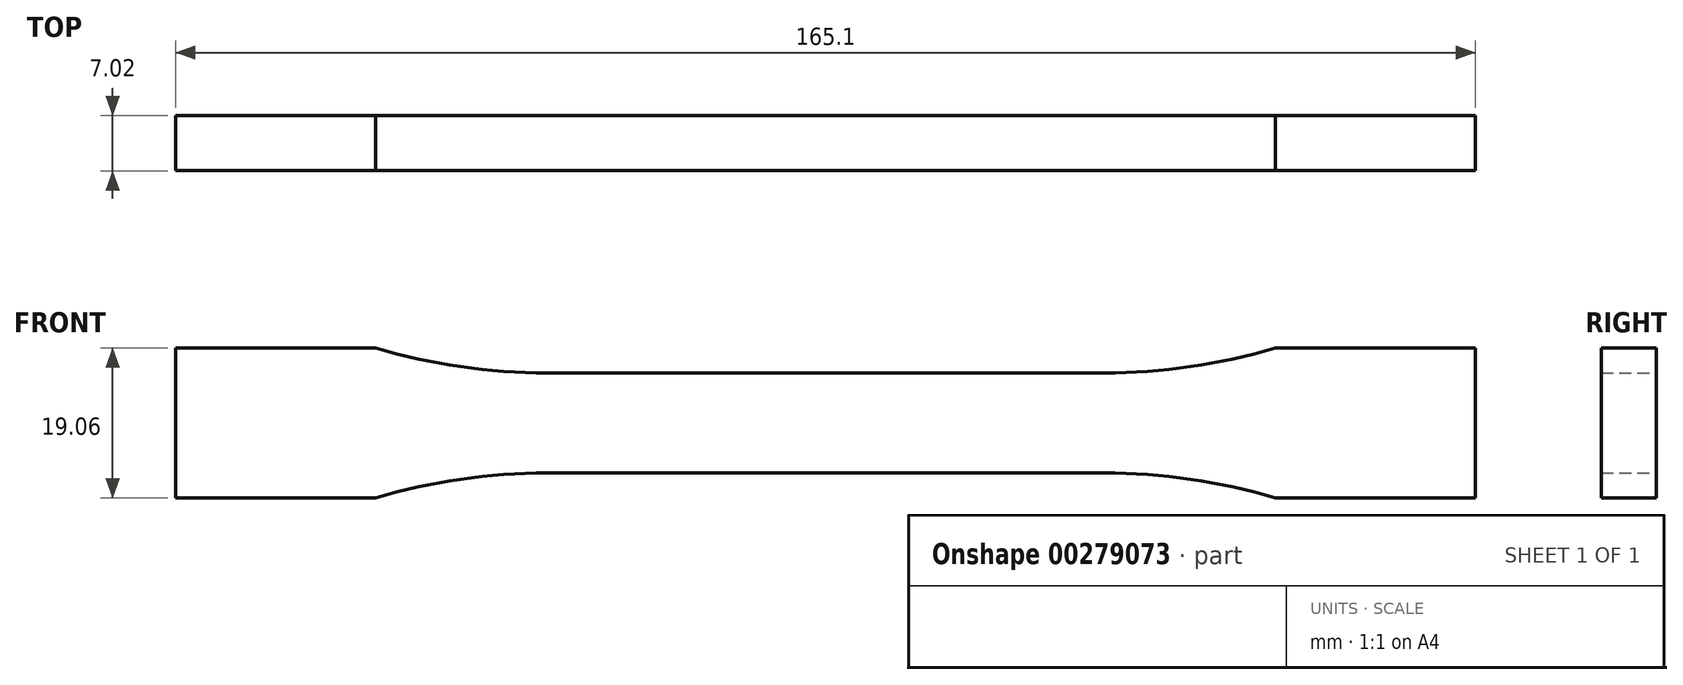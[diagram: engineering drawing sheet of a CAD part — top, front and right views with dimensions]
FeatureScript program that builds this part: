
annotation { "Feature Type Name" : "Feature", "Feature Type Description" : "" }
export const myFeature = defineFeature(function(context is Context, id is Id, definition is map)
    precondition{}
    {
        {
            var Q0;
            Q0=qCreatedBy(makeId("Front.planeOp"),FACE);
            var sketch = newSketch(context, id + "F0", { "sketchPlane" : qUnion([Q0])});
            skLineSegment(sketch, "E0", {"start": v(0, 6.35) * mm, "end": v(35.38, 6.35) * mm});
            skArc(sketch, "E1", {"start": v(35.38, 6.35) * mm, "mid": v(46.38, 7.15) * mm, "end": v(57.15, 9.53) * mm});
            skLineSegment(sketch, "E2", {"start": v(57.15, 9.53) * mm, "end": v(82.55, 9.53) * mm});
            skLineSegment(sketch, "E3.MirrorCS", {"start": v(57.15, -9.53) * mm, "end": v(82.55, -9.53) * mm});
            skLineSegment(sketch, "E4.MirrorCS", {"start": v(0, -6.35) * mm, "end": v(35.38, -6.35) * mm});
            skArc(sketch, "E5.MirrorCS", {"start": v(35.38, -6.35) * mm, "mid": v(46.38, -7.15) * mm, "end": v(57.15, -9.53) * mm});
            skArc(sketch, "E6.MirrorCS", {"start": v(-35.38, -6.35) * mm, "mid": v(-46.38, -7.15) * mm, "end": v(-57.15, -9.53) * mm});
            skLineSegment(sketch, "E7.MirrorCS", {"start": v(0, 6.35) * mm, "end": v(-35.38, 6.35) * mm});
            skArc(sketch, "E8.MirrorCS", {"start": v(-35.38, 6.35) * mm, "mid": v(-46.38, 7.15) * mm, "end": v(-57.15, 9.53) * mm});
            skLineSegment(sketch, "E9.MirrorCS", {"start": v(-57.15, -9.53) * mm, "end": v(-82.55, -9.53) * mm});
            skLineSegment(sketch, "E10.MirrorCS", {"start": v(0, -6.35) * mm, "end": v(-35.38, -6.35) * mm});
            skLineSegment(sketch, "E11.MirrorCS", {"start": v(-57.15, 9.53) * mm, "end": v(-82.55, 9.52) * mm});
            skLineSegment(sketch, "E12", {"start": v(82.55, 9.52) * mm, "end": v(82.55, -9.52) * mm});
            skLineSegment(sketch, "E13", {"start": v(-82.55, 9.52) * mm, "end": v(-82.55, -9.52) * mm});
            skSolve(sketch);
        }
        {
            var Q0;
            Q0=makeQuery(id+"F0.imprint","IMPRINT",FACE,{"disambiguationData":[TD([[makeQuery(id+"F0.imprint","IMPRINT",EDGE,{"derivedFrom":sQuery(id+"F0.wireOp",EDGE,"E0")}),-1.0]])]});
            extrude(context, id + "F1", {"entities" : qUnion([Q0]), "endBound" : BoundingType.SYMMETRIC, "depth" : 7 * mm});
        }
    });
